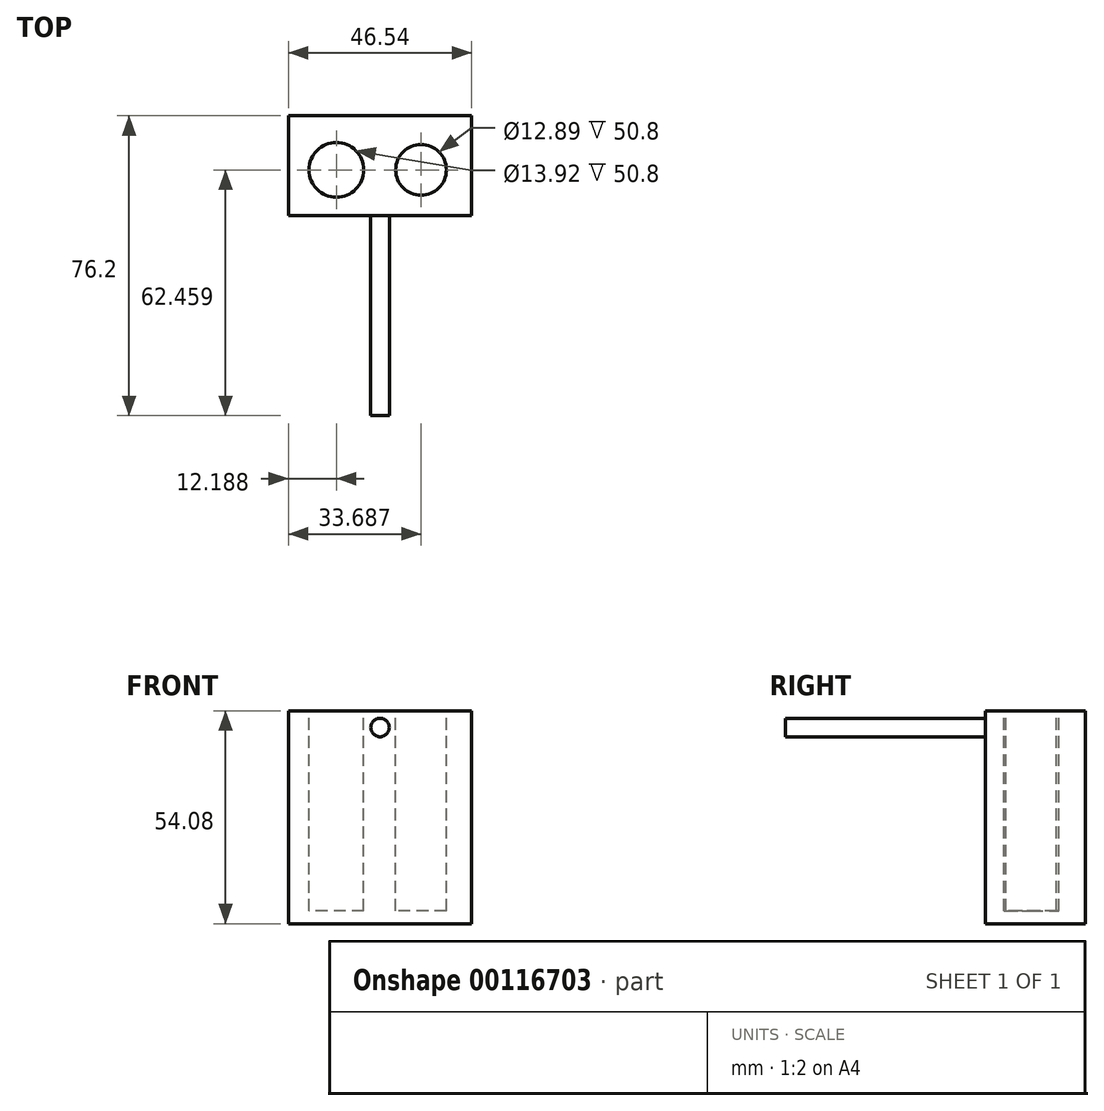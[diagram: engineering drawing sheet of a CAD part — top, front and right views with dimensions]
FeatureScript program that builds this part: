
annotation { "Feature Type Name" : "Feature", "Feature Type Description" : "" }
export const myFeature = defineFeature(function(context is Context, id is Id, definition is map)
    precondition{}
    {
        {
            var Q0;
            Q0=qCreatedBy(makeId("Front.planeOp"),FACE);
            var sketch = newSketch(context, id + "F0", { "sketchPlane" : qUnion([Q0])});
            skLineSegment(sketch, "E0.bottom", {"start": v(23.27, -27.04) * mm, "end": v(-23.27, -27.04) * mm});
            skLineSegment(sketch, "E0.top", {"start": v(23.27, 27.04) * mm, "end": v(-23.27, 27.04) * mm});
            skLineSegment(sketch, "E0.left", {"start": v(23.27, -27.04) * mm, "end": v(23.27, 27.04) * mm});
            skLineSegment(sketch, "E0.right", {"start": v(-23.27, -27.04) * mm, "end": v(-23.27, 27.04) * mm});
            skPoint(sketch, "E0.middle", {"position": v(0, 0) * mm});
            skSolve(sketch);
        }
        {
            var Q0;
            Q0=makeQuery(id+"F0.imprint","IMPRINT",FACE,{"disambiguationData":[TD([[makeQuery(id+"F0.imprint","IMPRINT",EDGE,{"derivedFrom":sQuery(id+"F0.wireOp",EDGE,"E0.bottom")}),-1.0]])]});
            extrude(context, id + "F1", {"entities" : qUnion([Q0]), "depth" : 25.4 * mm});
        }
        {
            var Q0;
            Q0=makeQuery(id+"F1.opExtrude","SWEPT_FACE",FACE,{"disambiguationData":[OSD([sQuery(id+"F0.wireOp",EDGE,"E0.top")])]});
            var sketch = newSketch(context, id + "F2", { "sketchPlane" : qUnion([Q0])});
            skCircle(sketch, "E1", {"center": v(-11.08, -13.74) * mm, "radius": 6.96 * mm});
            skCircle(sketch, "E2", {"center": v(10.42, -13.74) * mm, "radius": 6.44 * mm});
            skSolve(sketch);
        }
        {
            var Q0;
            Q0=makeQuery(id+"F2.imprint","IMPRINT",FACE,{"disambiguationData":[TD([[makeQuery(id+"F2.imprint","IMPRINT",EDGE,{"derivedFrom":sQuery(id+"F2.wireOp",EDGE,"E1")}),1.0]])]});
            var Q1;
            Q1=makeQuery(id+"F2.imprint","IMPRINT",FACE,{"disambiguationData":[TD([[makeQuery(id+"F2.imprint","IMPRINT",EDGE,{"derivedFrom":sQuery(id+"F2.wireOp",EDGE,"E2")}),1.0]])]});
            var Q2;
            Q2=sQuery(id+"F2.wireOp",EDGE,"E1");
            var Q3;
            Q3=sQuery(id+"F2.wireOp",EDGE,"E2");
            extrude(context, id + "F3", {"entities" : qUnion([Q0, Q1]), "operationType" : NewBodyOperationType.REMOVE, "surfaceEntities" : qUnion([Q2, Q3]), "oppositeDirection" : true, "depth" : 50.8 * mm});
        }
        {
            var Q0;
            Q0=makeQuery(id+"F1.opExtrude","CAP_FACE",FACE,{"disambiguationData":[OSD([sQuery(id+"F0.wireOp",EDGE,"E0.bottom"),sQuery(id+"F0.wireOp",EDGE,"E0.top"),sQuery(id+"F0.wireOp",EDGE,"E0.left"),sQuery(id+"F0.wireOp",EDGE,"E0.right")])],"isStart":false});
            var sketch = newSketch(context, id + "F4", { "sketchPlane" : qUnion([Q0])});
            skCircle(sketch, "E3", {"center": v(0, 22.83) * mm, "radius": 2.36 * mm});
            skSolve(sketch);
        }
        {
            var Q0;
            Q0 = qSketchRegion(id + "F4", true);
            extrude(context, id + "F5", {"entities" : qUnion([Q0]), "operationType" : NewBodyOperationType.ADD, "depth" : 50.8 * mm});
        }
    });
